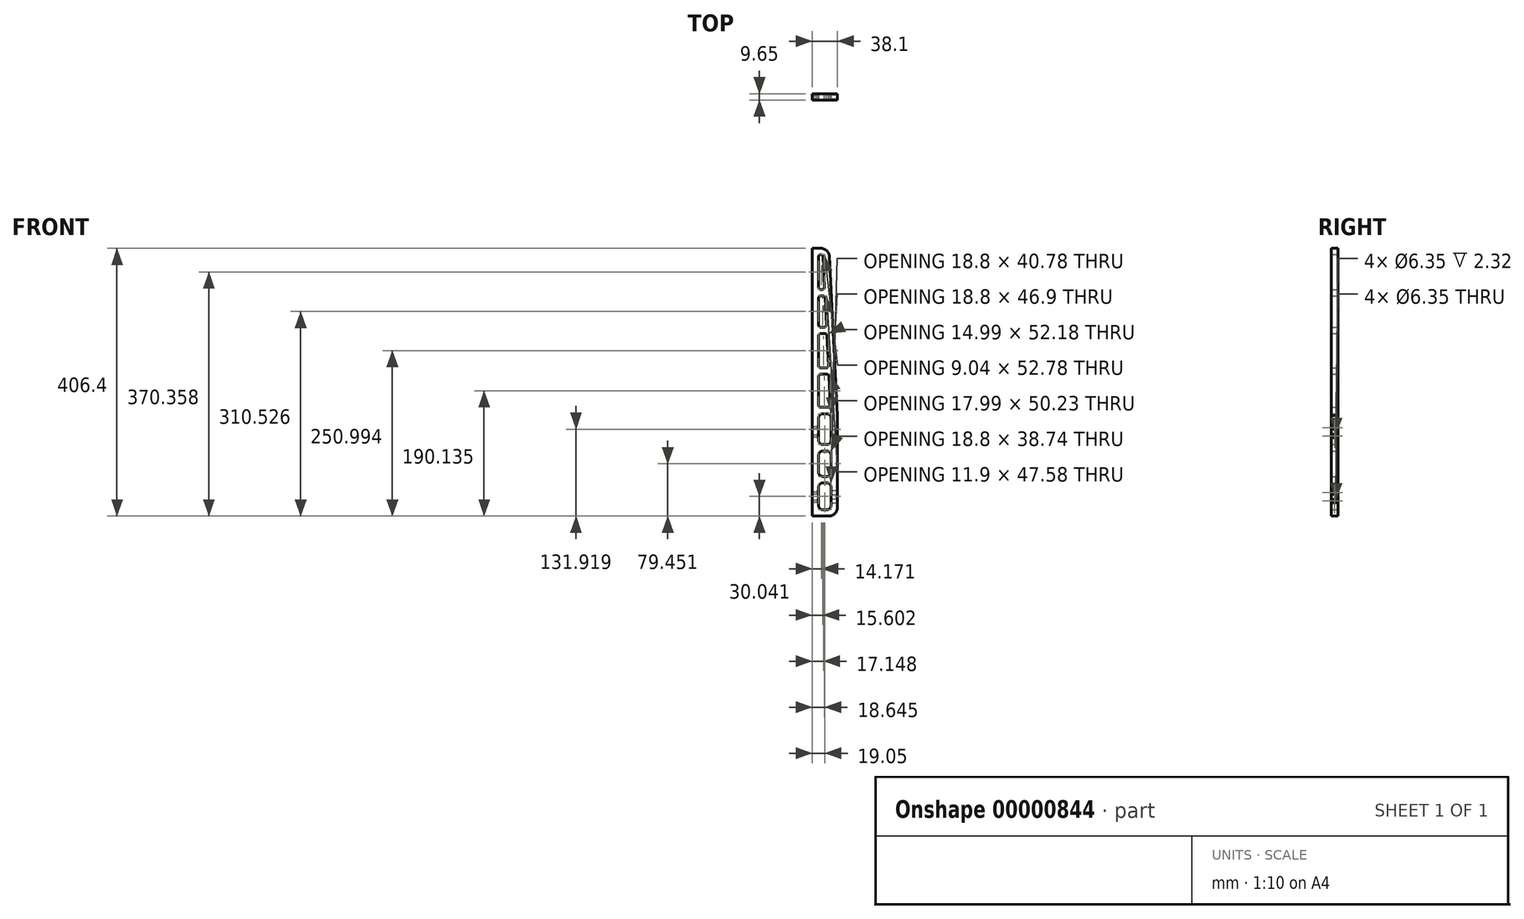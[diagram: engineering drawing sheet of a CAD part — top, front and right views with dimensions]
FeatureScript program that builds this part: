
annotation { "Feature Type Name" : "Feature", "Feature Type Description" : "" }
export const myFeature = defineFeature(function(context is Context, id is Id, definition is map)
    precondition{}
    {
        {
            var Q0;
            Q0=qCreatedBy(makeId("Front.planeOp"),FACE);
            var sketch = newSketch(context, id + "F0", { "sketchPlane" : qUnion([Q0])});
            skLineSegment(sketch, "E0", {"start": v(0, 0) * mm, "end": v(0, 406.4) * mm});
            skLineSegment(sketch, "E1", {"start": v(0, 406.4) * mm, "end": v(13.32, 406.4) * mm});
            skLineSegment(sketch, "E2", {"start": v(26, 394.33) * mm, "end": v(38.1, 152.4) * mm});
            skLineSegment(sketch, "E3", {"start": v(38.1, 152.4) * mm, "end": v(38.1, 12.7) * mm});
            skLineSegment(sketch, "E4", {"start": v(25.4, 0) * mm, "end": v(0, 0) * mm});
            skLineSegment(sketch, "E5.bottom", {"start": v(16, 155.37) * mm, "end": v(22.1, 155.37) * mm});
            skLineSegment(sketch, "E5.top", {"start": v(16, 9.65) * mm, "end": v(22.1, 9.65) * mm});
            skLineSegment(sketch, "E5.left", {"start": v(9.65, 149.02) * mm, "end": v(9.65, 114.82) * mm});
            skLineSegment(sketch, "E5.right", {"start": v(28.45, 149.02) * mm, "end": v(28.45, 114.82) * mm});
            skLineSegment(sketch, "E6", {"start": v(9.65, 273.9) * mm, "end": v(9.65, 228.08) * mm});
            skLineSegment(sketch, "E7", {"start": v(12.83, 224.9) * mm, "end": v(21.47, 224.9) * mm});
            skLineSegment(sketch, "E8", {"start": v(24.64, 228.24) * mm, "end": v(22.35, 274.07) * mm});
            skLineSegment(sketch, "E9", {"start": v(19.18, 277.08) * mm, "end": v(12.83, 277.08) * mm});
            skLineSegment(sketch, "E10", {"start": v(9.65, 393.57) * mm, "end": v(9.65, 347.14) * mm});
            skLineSegment(sketch, "E11", {"start": v(12.83, 343.97) * mm, "end": v(15.52, 343.97) * mm});
            skLineSegment(sketch, "E12", {"start": v(18.7, 347.3) * mm, "end": v(16.37, 393.73) * mm});
            skLineSegment(sketch, "E13", {"start": v(13.2, 396.75) * mm, "end": v(12.83, 396.75) * mm});
            skLineSegment(sketch, "E14", {"start": v(16, 108.47) * mm, "end": v(22.1, 108.47) * mm});
            skLineSegment(sketch, "E15", {"start": v(16, 50.43) * mm, "end": v(22.1, 50.43) * mm});
            skLineSegment(sketch, "E16.trimOffspring", {"start": v(28.45, 44.08) * mm, "end": v(28.45, 16) * mm});
            skLineSegment(sketch, "E17.trimOffspring", {"start": v(9.65, 44.08) * mm, "end": v(9.65, 16) * mm});
            skPoint(sketch, "E18.visualSharp", {"position": v(9.65, 9.65) * mm});
            skArc(sketch, "E18.filletArc", {"start": v(9.65, 16) * mm, "mid": v(11.51, 11.51) * mm, "end": v(16, 9.65) * mm});
            skPoint(sketch, "E19.visualSharp", {"position": v(28.45, 9.65) * mm});
            skArc(sketch, "E19.filletArc", {"start": v(22.1, 9.65) * mm, "mid": v(26.59, 11.51) * mm, "end": v(28.45, 16) * mm});
            skPoint(sketch, "E20.visualSharp", {"position": v(9.65, 50.43) * mm});
            skArc(sketch, "E20.filletArc", {"start": v(16, 50.43) * mm, "mid": v(11.51, 48.57) * mm, "end": v(9.65, 44.08) * mm});
            skPoint(sketch, "E21.visualSharp", {"position": v(28.45, 50.43) * mm});
            skArc(sketch, "E21.filletArc", {"start": v(28.45, 44.08) * mm, "mid": v(26.59, 48.57) * mm, "end": v(22.1, 50.43) * mm});
            skPoint(sketch, "E22.visualSharp", {"position": v(28.45, 108.47) * mm});
            skArc(sketch, "E22.filletArc", {"start": v(22.1, 108.47) * mm, "mid": v(26.59, 110.33) * mm, "end": v(28.45, 114.82) * mm});
            skArc(sketch, "E23.filletArc", {"start": v(28.45, 149.02) * mm, "mid": v(26.59, 153.5) * mm, "end": v(22.1, 155.37) * mm});
            skPoint(sketch, "E24.visualSharp", {"position": v(9.65, 155.37) * mm});
            skArc(sketch, "E24.filletArc", {"start": v(16, 155.37) * mm, "mid": v(11.51, 153.5) * mm, "end": v(9.65, 149.02) * mm});
            skPoint(sketch, "E25.visualSharp", {"position": v(9.65, 108.47) * mm});
            skArc(sketch, "E25.filletArc", {"start": v(9.65, 114.82) * mm, "mid": v(11.51, 110.33) * mm, "end": v(16, 108.47) * mm});
            skPoint(sketch, "E26.visualSharp", {"position": v(9.65, 224.9) * mm});
            skArc(sketch, "E26.filletArc", {"start": v(9.65, 228.08) * mm, "mid": v(10.58, 225.83) * mm, "end": v(12.83, 224.9) * mm});
            skPoint(sketch, "E27.visualSharp", {"position": v(9.65, 277.08) * mm});
            skArc(sketch, "E27.filletArc", {"start": v(12.83, 277.08) * mm, "mid": v(10.58, 276.15) * mm, "end": v(9.65, 273.9) * mm});
            skPoint(sketch, "E28.visualSharp", {"position": v(22.2, 277.08) * mm});
            skArc(sketch, "E28.filletArc", {"start": v(22.35, 274.07) * mm, "mid": v(21.37, 276.2) * mm, "end": v(19.18, 277.08) * mm});
            skPoint(sketch, "E29.visualSharp", {"position": v(24.81, 224.9) * mm});
            skArc(sketch, "E29.filletArc", {"start": v(21.47, 224.9) * mm, "mid": v(23.77, 225.9) * mm, "end": v(24.64, 228.24) * mm});
            skPoint(sketch, "E30.visualSharp", {"position": v(25.4, 406.4) * mm});
            skArc(sketch, "E30.filletArc", {"start": v(26, 394.33) * mm, "mid": v(22.07, 402.9) * mm, "end": v(13.32, 406.4) * mm});
            skPoint(sketch, "E31.visualSharp", {"position": v(18.86, 343.97) * mm});
            skArc(sketch, "E31.filletArc", {"start": v(15.52, 343.97) * mm, "mid": v(17.82, 344.95) * mm, "end": v(18.7, 347.3) * mm});
            skPoint(sketch, "E32.visualSharp", {"position": v(9.65, 343.97) * mm});
            skArc(sketch, "E32.filletArc", {"start": v(9.65, 347.14) * mm, "mid": v(10.58, 344.9) * mm, "end": v(12.83, 343.97) * mm});
            skPoint(sketch, "E33.visualSharp", {"position": v(9.65, 396.75) * mm});
            skArc(sketch, "E33.filletArc", {"start": v(12.83, 396.75) * mm, "mid": v(10.58, 395.82) * mm, "end": v(9.65, 393.57) * mm});
            skPoint(sketch, "E34.visualSharp", {"position": v(16.22, 396.75) * mm});
            skArc(sketch, "E34.filletArc", {"start": v(16.37, 393.73) * mm, "mid": v(15.39, 395.87) * mm, "end": v(13.2, 396.75) * mm});
            skArc(sketch, "E35.filletArc", {"start": v(24.47, 165.02) * mm, "mid": v(26.77, 166) * mm, "end": v(27.64, 168.35) * mm});
            skArc(sketch, "E36.filletArc", {"start": v(9.65, 168.2) * mm, "mid": v(10.58, 165.95) * mm, "end": v(12.83, 165.02) * mm});
            skLineSegment(sketch, "E37", {"start": v(9.65, 212.08) * mm, "end": v(9.65, 168.2) * mm});
            skLineSegment(sketch, "E38", {"start": v(27.64, 168.35) * mm, "end": v(25.44, 212.24) * mm});
            skArc(sketch, "E39.filletArc", {"start": v(25.44, 212.24) * mm, "mid": v(24.46, 214.38) * mm, "end": v(22.27, 215.25) * mm});
            skArc(sketch, "E40.filletArc", {"start": v(12.83, 215.25) * mm, "mid": v(10.58, 214.32) * mm, "end": v(9.65, 212.08) * mm});
            skLineSegment(sketch, "E41", {"start": v(22.27, 215.25) * mm, "end": v(12.83, 215.25) * mm});
            skLineSegment(sketch, "E42", {"start": v(12.83, 165.02) * mm, "end": v(24.47, 165.02) * mm});
            skLineSegment(sketch, "E43.top", {"start": v(16, 60.08) * mm, "end": v(22.1, 60.08) * mm});
            skArc(sketch, "E44.filletArc", {"start": v(9.65, 66.43) * mm, "mid": v(11.51, 61.94) * mm, "end": v(16, 60.08) * mm});
            skArc(sketch, "E45.filletArc", {"start": v(22.1, 60.08) * mm, "mid": v(26.59, 61.94) * mm, "end": v(28.45, 66.43) * mm});
            skLineSegment(sketch, "E46.trimOffspring", {"start": v(28.45, 92.47) * mm, "end": v(28.45, 66.43) * mm});
            skArc(sketch, "E47.filletArc", {"start": v(28.45, 92.47) * mm, "mid": v(26.59, 96.96) * mm, "end": v(22.1, 98.82) * mm});
            skLineSegment(sketch, "E48", {"start": v(16, 98.82) * mm, "end": v(22.1, 98.82) * mm});
            skArc(sketch, "E49.filletArc", {"start": v(16, 98.82) * mm, "mid": v(11.51, 96.96) * mm, "end": v(9.65, 92.47) * mm});
            skLineSegment(sketch, "E50.trimOffspring", {"start": v(9.65, 92.47) * mm, "end": v(9.65, 66.43) * mm});
            skLineSegment(sketch, "E51", {"start": v(16.32, 334.32) * mm, "end": v(12.83, 334.32) * mm});
            skArc(sketch, "E52.filletArc", {"start": v(12.83, 334.32) * mm, "mid": v(10.58, 333.39) * mm, "end": v(9.65, 331.14) * mm});
            skArc(sketch, "E53.filletArc", {"start": v(19.5, 331.3) * mm, "mid": v(18.5, 333.44) * mm, "end": v(16.32, 334.32) * mm});
            skLineSegment(sketch, "E54", {"start": v(9.65, 331.14) * mm, "end": v(9.65, 289.91) * mm});
            skLineSegment(sketch, "E55", {"start": v(21.55, 290.07) * mm, "end": v(19.5, 331.3) * mm});
            skLineSegment(sketch, "E56", {"start": v(12.83, 286.74) * mm, "end": v(18.38, 286.74) * mm});
            skArc(sketch, "E57.filletArc", {"start": v(9.65, 289.91) * mm, "mid": v(10.58, 287.67) * mm, "end": v(12.83, 286.74) * mm});
            skArc(sketch, "E58.filletArc", {"start": v(18.38, 286.74) * mm, "mid": v(20.68, 287.72) * mm, "end": v(21.55, 290.07) * mm});
            skPoint(sketch, "E59.visualSharp", {"position": v(38.1, 0) * mm});
            skArc(sketch, "E59.filletArc", {"start": v(25.4, 0) * mm, "mid": v(34.38, 3.72) * mm, "end": v(38.1, 12.7) * mm});
            skSolve(sketch);
        }
        {
            var Q0;
            Q0=makeQuery(id+"F0.imprint","IMPRINT",FACE,{"disambiguationData":[TD([[makeQuery(id+"F0.imprint","IMPRINT",EDGE,{"derivedFrom":sQuery(id+"F0.wireOp",EDGE,"E0")}),-1.0]])]});
            extrude(context, id + "F1", {"entities" : qUnion([Q0]), "depth" : 9.65 * mm});
        }
        {
            var Q0;
            Q0=makeQuery(id+"F1.opExtrude","SWEPT_FACE",FACE,{"disambiguationData":[OSD([sQuery(id+"F0.wireOp",EDGE,"E3")])]});
            var sketch = newSketch(context, id + "F2", { "sketchPlane" : qUnion([Q0])});
            skLineSegment(sketch, "E60", {"start": v(-4.83, 0) * mm, "end": v(-4.83, 152.4) * mm, "construction": true});
            skLineSegment(sketch, "E61", {"start": v(-4.83, 152.4) * mm, "end": v(-4.83, 203.99) * mm, "construction": true});
            skCircle(sketch, "E62", {"center": v(-4.83, 35.5) * mm, "radius": 1.59 * mm});
            skCircle(sketch, "E63", {"center": v(-4.83, 134.25) * mm, "radius": 1.59 * mm});
            skCircle(sketch, "E64", {"center": v(-4.83, 121.55) * mm, "radius": 1.59 * mm});
            skCircle(sketch, "E65", {"center": v(-4.83, 22.8) * mm, "radius": 1.59 * mm});
            skSolve(sketch);
        }
        {
            var Q0;
            Q0 = qSketchRegion(id + "F2", true);
            var Q1;
            Q1=makeQuery(id+"F1.opExtrude","SWEPT_FACE",FACE,{"disambiguationData":[OSD([sQuery(id+"F0.wireOp",EDGE,"E0")])]});
            extrude(context, id + "F3", {"entities" : qUnion([Q0]), "operationType" : NewBodyOperationType.REMOVE, "endBound" : BoundingType.UP_TO_SURFACE, "oppositeDirection" : true, "endBoundEntityFace" : qUnion([Q1]), "depth" : 25.4 * mm});
        }
        {
            var Q0;
            Q0=makeQuery(id+"F1.opExtrude","SWEPT_FACE",FACE,{"disambiguationData":[OSD([sQuery(id+"F0.wireOp",EDGE,"E3")])]});
            var sketch = newSketch(context, id + "F4", { "sketchPlane" : qUnion([Q0])});
            skCircle(sketch, "E66", {"center": v(-4.83, 134.25) * mm, "radius": 3.18 * mm});
            skCircle(sketch, "E67", {"center": v(-4.83, 121.55) * mm, "radius": 3.18 * mm});
            skCircle(sketch, "E68", {"center": v(-4.83, 35.5) * mm, "radius": 3.18 * mm});
            skCircle(sketch, "E69", {"center": v(-4.83, 22.8) * mm, "radius": 3.18 * mm});
            skSolve(sketch);
        }
        {
            var Q0;
            Q0 = qSketchRegion(id + "F4", true);
            var Q1;
            Q1=makeQuery(id+"F1.opExtrude","SWEPT_FACE",FACE,{"disambiguationData":[OSD([sQuery(id+"F0.wireOp",EDGE,"E5.left")])]});
            extrude(context, id + "F5", {"entities" : qUnion([Q0]), "operationType" : NewBodyOperationType.REMOVE, "oppositeDirection" : true, "endBoundEntity" : qUnion([Q1]), "depth" : 30.77 * mm});
        }
    });
